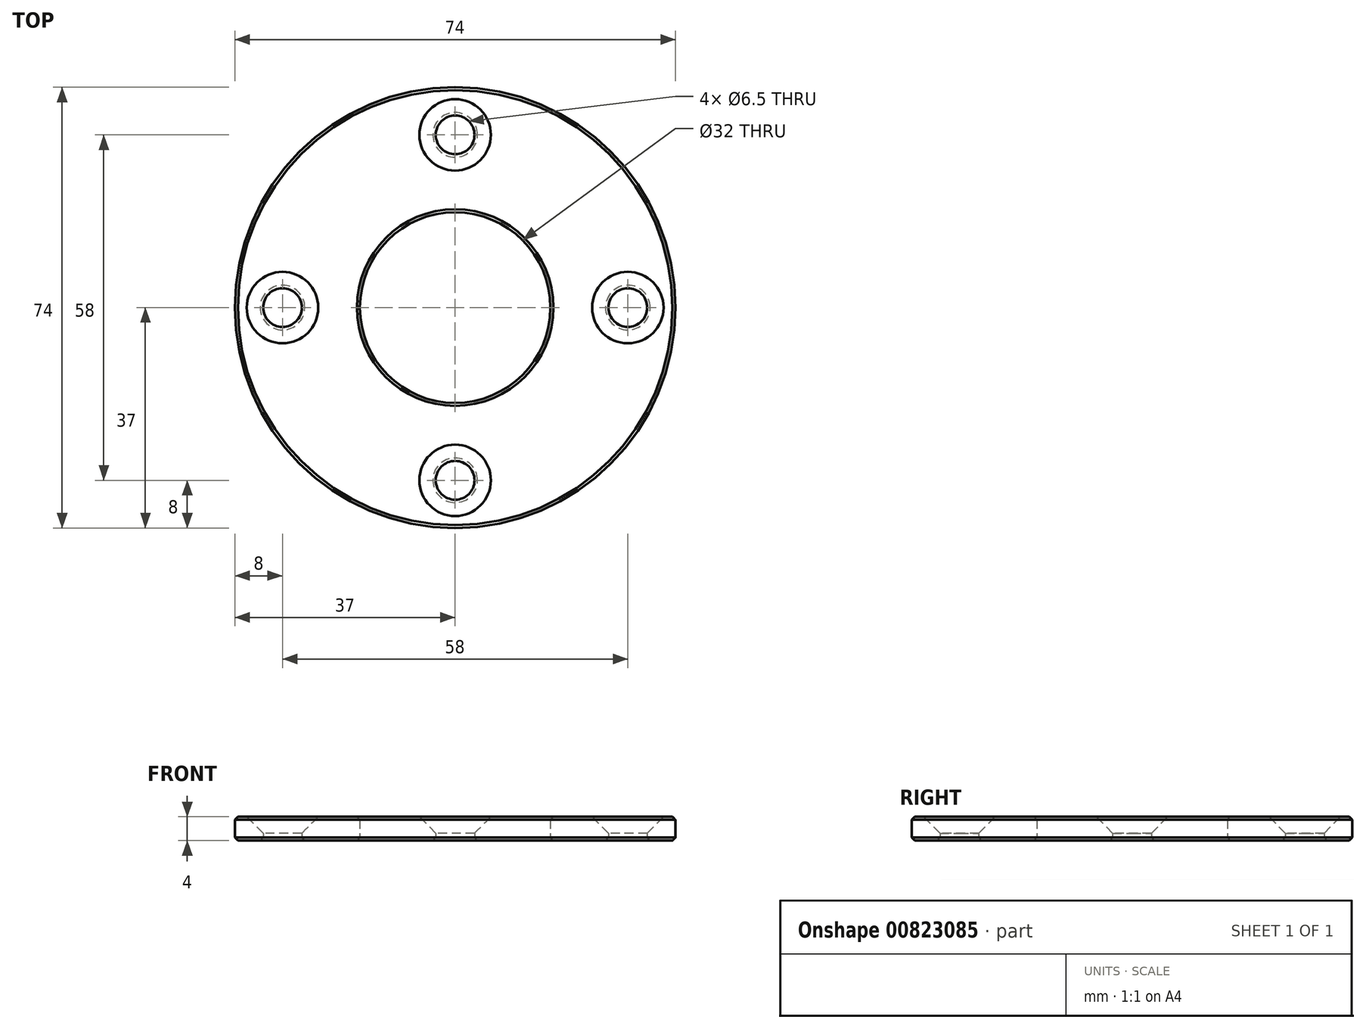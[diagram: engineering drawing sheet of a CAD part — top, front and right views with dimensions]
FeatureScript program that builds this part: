
annotation { "Feature Type Name" : "Feature", "Feature Type Description" : "" }
export const myFeature = defineFeature(function(context is Context, id is Id, definition is map)
    precondition{}
    {
        {
            var Q0;
            Q0=qCreatedBy(makeId("Top.planeOp"),FACE);
            var sketch = newSketch(context, id + "F0", { "sketchPlane" : qUnion([Q0])});
            skCircle(sketch, "E0", {"center": v(0, 0) * mm, "radius": 16 * mm});
            skCircle(sketch, "E1", {"center": v(0, 0) * mm, "radius": 29 * mm, "construction": true});
            skCircle(sketch, "E2", {"center": v(0, 0) * mm, "radius": 37 * mm});
            skLineSegment(sketch, "E3", {"start": v(0, -37) * mm, "end": v(0, 37) * mm, "construction": true});
            skLineSegment(sketch, "E4", {"start": v(0, 37) * mm, "end": v(37, 0) * mm, "construction": true});
            skLineSegment(sketch, "E5", {"start": v(37, 0) * mm, "end": v(-37, 0) * mm, "construction": true});
            skCircle(sketch, "E6", {"center": v(0, 29) * mm, "radius": 3.25 * mm});
            skCircle(sketch, "E7", {"center": v(-29, 0) * mm, "radius": 3.25 * mm});
            skCircle(sketch, "E8", {"center": v(0, -29) * mm, "radius": 3.25 * mm});
            skCircle(sketch, "E9", {"center": v(29, 0) * mm, "radius": 3.25 * mm});
            skSolve(sketch);
        }
        {
            var Q0;
            Q0=qSketchRegion(id+"F0",true);
            extrude(context, id + "F1", {"entities" : qUnion([Q0]), "depth" : 4 * mm, "offsetDistance" : 25 * mm});
        }
        {
            var Q0;
            Q0=makeQuery(id+"F1.opExtrude","CAP_EDGE",EDGE,{"disambiguationData":[OSD([sQuery(id+"F0.wireOp",EDGE,"E8")])],"isStart":false});
            var Q1;
            Q1=makeQuery(id+"F1.opExtrude","CAP_EDGE",EDGE,{"disambiguationData":[OSD([sQuery(id+"F0.wireOp",EDGE,"E7")])],"isStart":false});
            var Q2;
            Q2=makeQuery(id+"F1.opExtrude","CAP_EDGE",EDGE,{"disambiguationData":[OSD([sQuery(id+"F0.wireOp",EDGE,"E6")])],"isStart":false});
            var Q3;
            Q3=makeQuery(id+"F1.opExtrude","CAP_EDGE",EDGE,{"disambiguationData":[OSD([sQuery(id+"F0.wireOp",EDGE,"E9")])],"isStart":false});
            chamfer(context, id + "F2", {"entities" : qUnion([Q0, Q1, Q2, Q3]), "width" : 2.75 * mm, "tangentPropagation" : true});
        }
        {
            var Q0;
            Q0=makeQuery(id+"F1.opExtrude","SWEPT_FACE",FACE,{"disambiguationData":[OSD([sQuery(id+"F0.wireOp",EDGE,"E0")])]});
            var Q1;
            Q1=makeQuery(id+"F1.opExtrude","SWEPT_FACE",FACE,{"disambiguationData":[OSD([sQuery(id+"F0.wireOp",EDGE,"E2")])]});
            var Q2;
            Q2=makeQuery(id+"F1.opExtrude","CAP_FACE",FACE,{"disambiguationData":[OSD([sQuery(id+"F0.wireOp",EDGE,"E0"),sQuery(id+"F0.wireOp",EDGE,"E2"),sQuery(id+"F0.wireOp",EDGE,"E6"),sQuery(id+"F0.wireOp",EDGE,"E7"),sQuery(id+"F0.wireOp",EDGE,"E8"),sQuery(id+"F0.wireOp",EDGE,"E9")])],"isStart":true});
            chamfer(context, id + "F3", {"entities" : qUnion([Q0, Q1, Q2]), "width" : 0.5 * mm, "tangentPropagation" : true});
        }
    });
